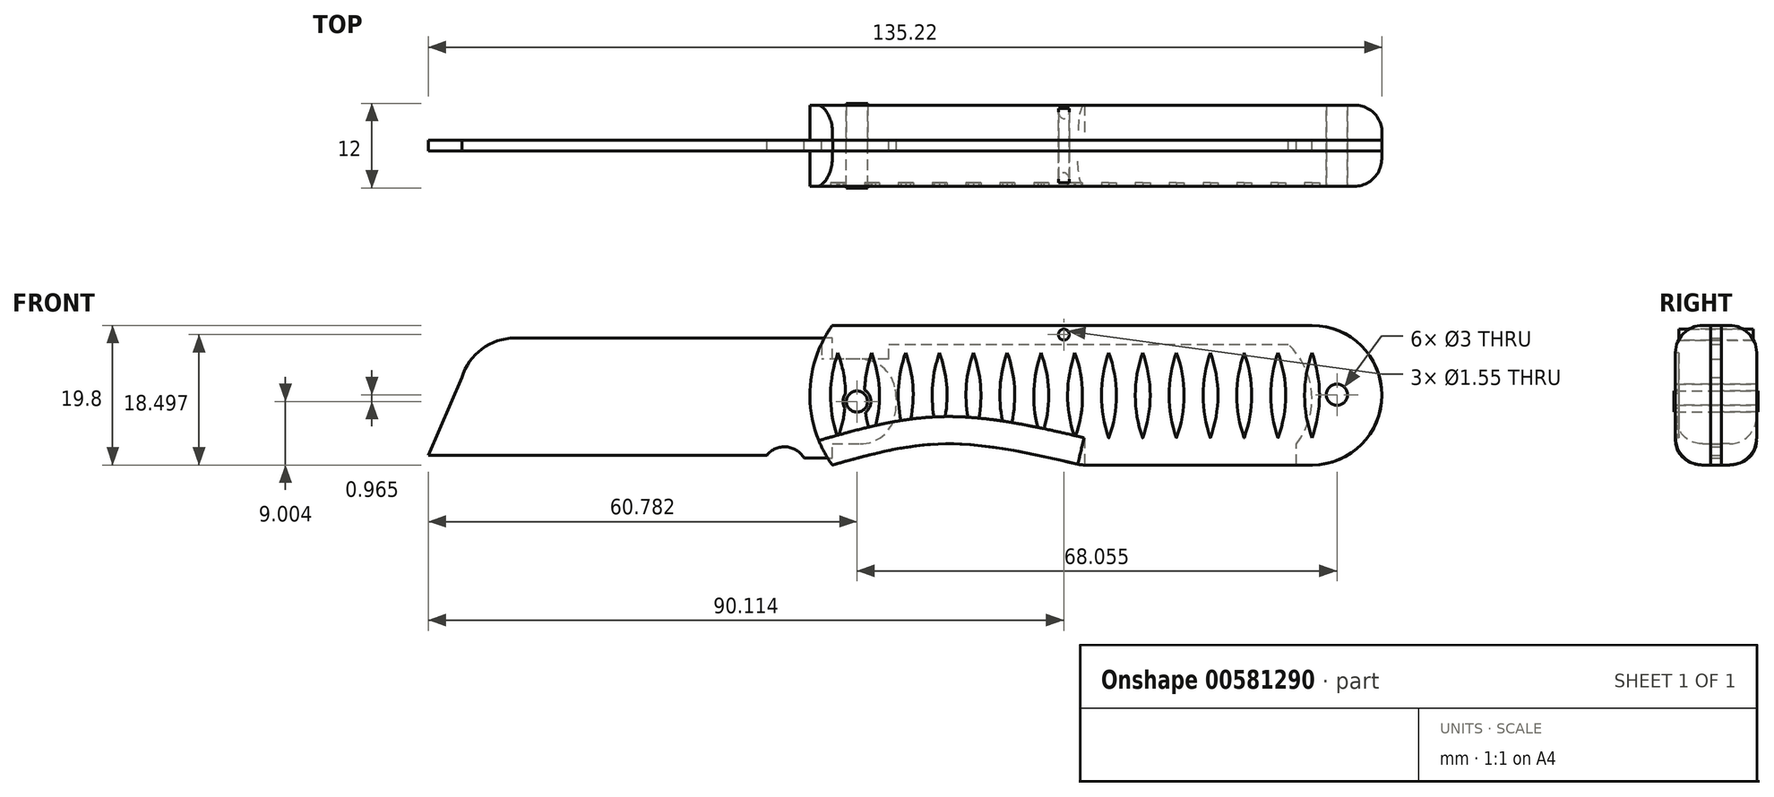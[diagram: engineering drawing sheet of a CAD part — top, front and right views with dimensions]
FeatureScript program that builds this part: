
annotation { "Feature Type Name" : "Feature", "Feature Type Description" : "" }
export const myFeature = defineFeature(function(context is Context, id is Id, definition is map)
    precondition{}
    {
        {
            var Q0;
            Q0=qCreatedBy(makeId("Front.planeOp"),FACE);
            var sketch = newSketch(context, id + "F0", { "sketchPlane" : qUnion([Q0])});
            skLineSegment(sketch, "E0", {"start": v(-36.7, 0) * mm, "end": v(11.3, 0) * mm});
            skArc(sketch, "E1", {"start": v(16.58, -0.4) * mm, "mid": v(14.04, 1.17) * mm, "end": v(11.3, 0) * mm});
            skLineSegment(sketch, "E2", {"start": v(16.58, -0.4) * mm, "end": v(20.58, -0.4) * mm});
            skLineSegment(sketch, "E3", {"start": v(20.58, -0.4) * mm, "end": v(20.58, 1.6) * mm});
            skLineSegment(sketch, "E4", {"start": v(20.58, 1.6) * mm, "end": v(27.58, 1.6) * mm});
            skLineSegment(sketch, "E5", {"start": v(27.58, 13.6) * mm, "end": v(20.58, 13.6) * mm});
            skArc(sketch, "E6", {"start": v(27.58, 1.6) * mm, "mid": v(29.67, 7.6) * mm, "end": v(27.58, 13.6) * mm});
            skLineSegment(sketch, "E7", {"start": v(20.58, 13.6) * mm, "end": v(20.58, 16.6) * mm});
            skCircle(sketch, "E8", {"center": v(24.08, 7.6) * mm, "radius": 1.5 * mm});
            skLineSegment(sketch, "E9", {"start": v(20.58, 16.6) * mm, "end": v(-24.42, 16.6) * mm});
            skArc(sketch, "E10", {"start": v(-24.42, 16.6) * mm, "mid": v(-29.1, 15.05) * mm, "end": v(-31.92, 11) * mm});
            skLineSegment(sketch, "E11", {"start": v(-31.92, 11) * mm, "end": v(-36.7, 0) * mm});
            skPoint(sketch, "E12.end.orphan", {"position": v(16.3, 0) * mm});
            skPoint(sketch, "E13.orphan", {"position": v(24.08, 13.6) * mm});
            skSolve(sketch);
        }
        {
            var Q0;
            Q0 = qSketchRegion(id + "F0", true);
            extrude(context, id + "F1", {"entities" : qUnion([Q0]), "endBound" : BoundingType.SYMMETRIC, "depth" : 1.5 * mm, "offsetDistance" : 25 * mm});
        }
        {
            var Q0;
            Q0=makeQuery(id+"F1.opExtrude","CAP_FACE",FACE,{"disambiguationData":[OSD([sQuery(id+"F0.wireOp",EDGE,"E0"),sQuery(id+"F0.wireOp",EDGE,"E1"),sQuery(id+"F0.wireOp",EDGE,"E2"),sQuery(id+"F0.wireOp",EDGE,"E3"),sQuery(id+"F0.wireOp",EDGE,"E4"),sQuery(id+"F0.wireOp",EDGE,"E5"),sQuery(id+"F0.wireOp",EDGE,"E6"),sQuery(id+"F0.wireOp",EDGE,"E7"),sQuery(id+"F0.wireOp",EDGE,"E8"),sQuery(id+"F0.wireOp",EDGE,"E9"),sQuery(id+"F0.wireOp",EDGE,"E10"),sQuery(id+"F0.wireOp",EDGE,"E11")])],"isStart":false});
            var sketch = newSketch(context, id + "F2", { "sketchPlane" : qUnion([Q0])});
            skCircle(sketch, "E14", {"center": v(24.08, 7.6) * mm, "radius": 1.5 * mm});
            skLineSegment(sketch, "E15", {"start": v(17.43, 7.6) * mm, "end": v(33.27, 7.6) * mm});
            skPoint(sketch, "E16.MirrorCS.end.orphan", {"position": v(17.43, 7.6) * mm});
            skLineSegment(sketch, "E17", {"start": v(55.83, -1.4) * mm, "end": v(88.58, -1.4) * mm});
            skFitSpline(sketch, "E18", {"points": [v(20.58, -1.4) * mm, v(36.47, 1.6) * mm, v(55.83, -1.4) * mm], "startDerivative": vector(32.52, 9.17) * mm, "endDerivative": vector(37.9, -8.88) * mm});
            skLineSegment(sketch, "E19.MirrorCS", {"start": v(20.58, 18.4) * mm, "end": v(88.58, 18.4) * mm});
            skArc(sketch, "E20", {"start": v(20.58, 18.4) * mm, "mid": v(17.4, 8.5) * mm, "end": v(20.58, -1.4) * mm});
            skArc(sketch, "E21", {"start": v(88.58, -1.4) * mm, "mid": v(98.48, 8.5) * mm, "end": v(88.58, 18.4) * mm});
            skSolve(sketch);
        }
        {
            var Q0;
            Q0 = qSketchRegion(id + "F2", true);
            extrude(context, id + "F3", {"entities" : qUnion([Q0]), "depth" : 5 * mm, "offsetDistance" : 25 * mm});
        }
        {
            var Q0;
            Q0=makeQuery(id+"F3.opExtrude","CAP_EDGE",EDGE,{"disambiguationData":[OSD([sQuery(id+"F2.wireOp",EDGE,"E18")])],"isStart":false});
            fillet(context, id + "F4", {"entities" : qUnion([Q0]), "radius" : 3.86 * mm, "tangentPropagation" : true, "allowEdgeOverflow" : false});
        }
        {
            var Q0;
            Q0=makeQuery(id+"F3.opExtrude","CAP_EDGE",EDGE,{"disambiguationData":[OSD([sQuery(id+"F2.wireOp",EDGE,"E17")])],"isStart":false});
            fillet(context, id + "F5", {"entities" : qUnion([Q0]), "radius" : 3.86 * mm, "tangentPropagation" : true, "allowEdgeOverflow" : false});
        }
        {
            var Q0;
            Q0=makeQuery(id+"F1.opExtrude","CAP_FACE",FACE,{"disambiguationData":[OSD([sQuery(id+"F0.wireOp",EDGE,"E0"),sQuery(id+"F0.wireOp",EDGE,"E1"),sQuery(id+"F0.wireOp",EDGE,"E2"),sQuery(id+"F0.wireOp",EDGE,"E3"),sQuery(id+"F0.wireOp",EDGE,"E4"),sQuery(id+"F0.wireOp",EDGE,"E5"),sQuery(id+"F0.wireOp",EDGE,"E6"),sQuery(id+"F0.wireOp",EDGE,"E7"),sQuery(id+"F0.wireOp",EDGE,"E8"),sQuery(id+"F0.wireOp",EDGE,"E9"),sQuery(id+"F0.wireOp",EDGE,"E10"),sQuery(id+"F0.wireOp",EDGE,"E11")])],"isStart":true});
            var sketch = newSketch(context, id + "F6", { "sketchPlane" : qUnion([Q0])});
            skCircle(sketch, "E22.MirrorC", {"center": v(-24.08, 7.6) * mm, "radius": 1.5 * mm});
            skLineSegment(sketch, "E23.MirrorCS", {"start": v(-55.87, -1.4) * mm, "end": v(-88.62, -1.4) * mm});
            skFitSpline(sketch, "E24.MirrorCS", {"points": [v(-20.62, -1.4) * mm, v(-36.5, 1.6) * mm, v(-55.87, -1.4) * mm], "startDerivative": vector(-32.52, 9.17) * mm, "endDerivative": vector(-37.9, -8.88) * mm});
            skLineSegment(sketch, "E25.MirrorCS", {"start": v(-20.62, 18.4) * mm, "end": v(-88.62, 18.4) * mm});
            skArc(sketch, "E26.MirrorCS", {"start": v(-20.62, 18.4) * mm, "mid": v(-17.45, 8.5) * mm, "end": v(-20.62, -1.4) * mm});
            skArc(sketch, "E27.MirrorCS", {"start": v(-88.62, -1.4) * mm, "mid": v(-98.52, 8.5) * mm, "end": v(-88.62, 18.4) * mm});
            skLineSegment(sketch, "E28.MirrorCS", {"start": v(-17.47, 7.6) * mm, "end": v(-33.31, 7.6) * mm});
            skSolve(sketch);
        }
        {
            var Q0;
            Q0 = qSketchRegion(id + "F6", true);
            extrude(context, id + "F7", {"entities" : qUnion([Q0]), "depth" : 5 * mm, "offsetDistance" : 25 * mm});
        }
        {
            var Q0;
            Q0=makeQuery(id+"F7.opExtrude","CAP_EDGE",EDGE,{"disambiguationData":[OSD([sQuery(id+"F6.wireOp",EDGE,"a4459e08-6a74-43f8-8a37-8007887f801a2.MirrorCS")])],"isStart":false});
            var Q1;
            Q1=makeQuery(id+"F7.opExtrude","CAP_EDGE",EDGE,{"disambiguationData":[OSD([sQuery(id+"F6.wireOp",EDGE,"205b8de5-6952-42f7-a2c1-d582361c57c33.MirrorCS")])],"isStart":false});
            var Q2;
            Q2=makeQuery(id+"F7.opExtrude","CAP_EDGE",EDGE,{"disambiguationData":[OSD([sQuery(id+"F6.wireOp",EDGE,"E24.MirrorCS")])],"isStart":false});
            fillet(context, id + "F8", {"entities" : qUnion([Q0, Q1, Q2]), "radius" : 3.86 * mm, "tangentPropagation" : true, "allowEdgeOverflow" : false});
        }
        {
            var Q0;
            Q0=makeQuery(id+"F7.opExtrude","CAP_EDGE",EDGE,{"disambiguationData":[OSD([sQuery(id+"F6.wireOp",EDGE,"a4459e08-6a74-43f8-8a37-8007887f801a3.MirrorCS")])],"isStart":false});
            var Q1;
            Q1=makeQuery(id+"F7.opExtrude","CAP_EDGE",EDGE,{"disambiguationData":[OSD([sQuery(id+"F6.wireOp",EDGE,"205b8de5-6952-42f7-a2c1-d582361c57c32.MirrorCS")])],"isStart":false});
            var Q2;
            Q2=makeQuery(id+"F7.opExtrude","CAP_EDGE",EDGE,{"disambiguationData":[OSD([sQuery(id+"F6.wireOp",EDGE,"E23.MirrorCS")])],"isStart":false});
            fillet(context, id + "F9", {"entities" : qUnion([Q0, Q1, Q2]), "radius" : 3.86 * mm, "tangentPropagation" : true, "allowEdgeOverflow" : false});
        }
        {
            var Q0;
            Q0=makeQuery(id+"F0.imprint","IMPRINT",FACE,{"disambiguationData":[TD([[makeQuery(id+"F0.imprint","IMPRINT",EDGE,{"derivedFrom":sQuery(id+"F0.wireOp",EDGE,"E8")}),1.0]])]});
            extrude(context, id + "F10", {"entities" : qUnion([Q0]), "endBound" : BoundingType.SYMMETRIC, "depth" : 12 * mm, "offsetDistance" : 25 * mm});
        }
        {
            var Q0;
            Q0=qCreatedBy(makeId("Front.planeOp"),FACE);
            var sketch = newSketch(context, id + "F11", { "sketchPlane" : qUnion([Q0])});
            skLineSegment(sketch, "E29", {"start": v(22.62, 18.4) * mm, "end": v(84.2, 18.4) * mm});
            skPoint(sketch, "E30.orphan", {"position": v(53.4, 18.4) * mm});
            skPoint(sketch, "E31.end.orphan", {"position": v(87.09, 16.63) * mm});
            skLineSegment(sketch, "E32", {"start": v(84.2, 18.4) * mm, "end": v(88.58, 18.4) * mm});
            skArc(sketch, "E33", {"start": v(88.58, -1.4) * mm, "mid": v(98.48, 8.5) * mm, "end": v(88.58, 18.4) * mm});
            skLineSegment(sketch, "E34", {"start": v(20.58, 13.6) * mm, "end": v(27.58, 13.6) * mm});
            skLineSegment(sketch, "E35", {"start": v(28.58, 15.72) * mm, "end": v(84.2, 15.72) * mm});
            skLineSegment(sketch, "E36", {"start": v(86.4, -1.4) * mm, "end": v(88.58, -1.4) * mm});
            skLineSegment(sketch, "E37", {"start": v(86.4, -1.4) * mm, "end": v(86.4, 1.57) * mm});
            skPoint(sketch, "E38.orphan", {"position": v(84.2, -1.4) * mm});
            skLineSegment(sketch, "E39", {"start": v(84.2, 15.72) * mm, "end": v(85.2, 15.72) * mm});
            skArc(sketch, "E40", {"start": v(86.4, 1.57) * mm, "mid": v(88.56, 8.87) * mm, "end": v(85.2, 15.72) * mm});
            skLineSegment(sketch, "E41", {"start": v(20.58, 13.6) * mm, "end": v(19.04, 13.6) * mm});
            skPoint(sketch, "E42.start.orphan", {"position": v(20.58, 16.6) * mm});
            skLineSegment(sketch, "E43", {"start": v(27.58, 13.6) * mm, "end": v(28.58, 13.6) * mm});
            skLineSegment(sketch, "E44", {"start": v(28.58, 13.6) * mm, "end": v(28.58, 15.72) * mm});
            skPoint(sketch, "E45.end.orphan", {"position": v(18.58, 16.6) * mm});
            skLineSegment(sketch, "E46", {"start": v(22.62, 18.4) * mm, "end": v(20.65, 18.4) * mm});
            skLineSegment(sketch, "E47", {"start": v(19.04, 15.72) * mm, "end": v(19.04, 13.6) * mm});
            skPoint(sketch, "E48.orphan", {"position": v(18.58, 13.6) * mm});
            skArc(sketch, "E49", {"start": v(20.65, 18.4) * mm, "mid": v(19.78, 17.1) * mm, "end": v(19.04, 15.72) * mm});
            skSolve(sketch);
        }
        {
            var Q0;
            Q0 = qSketchRegion(id + "F11", true);
            extrude(context, id + "F12", {"entities" : qUnion([Q0]), "endBound" : BoundingType.SYMMETRIC, "depth" : 1.5 * mm, "offsetDistance" : 25 * mm});
        }
        {
            var Q0;
            Q0=qCreatedBy(makeId("Front.planeOp"),FACE);
            var sketch = newSketch(context, id + "F13", { "sketchPlane" : qUnion([Q0])});
            skCircle(sketch, "E50", {"center": v(53.41, 17.1) * mm, "radius": 0.78 * mm});
            skSolve(sketch);
        }
        {
            var Q0;
            Q0 = qSketchRegion(id + "F13", true);
            extrude(context, id + "F14", {"entities" : qUnion([Q0]), "operationType" : NewBodyOperationType.REMOVE, "endBound" : BoundingType.SYMMETRIC, "oppositeDirection" : true, "depth" : 25 * mm, "offsetDistance" : 25 * mm});
        }
        {
            var Q0;
            Q0 = qSketchRegion(id + "F13", true);
            extrude(context, id + "F15", {"entities" : qUnion([Q0]), "endBound" : BoundingType.SYMMETRIC, "depth" : 10.54 * mm, "offsetDistance" : 25 * mm});
        }
        {
            var Q0;
            Q0=makeQuery(id+"F1.opExtrude","SWEPT_EDGE",EDGE,{"disambiguationData":[OSD([sQuery(id+"F0.wireOp",EDGE,"E5"),sQuery(id+"F0.wireOp",EDGE,"E6")])]});
            var Q1;
            Q1=makeQuery(id+"F1.opExtrude","SWEPT_EDGE",EDGE,{"disambiguationData":[OSD([sQuery(id+"F0.wireOp",EDGE,"E4"),sQuery(id+"F0.wireOp",EDGE,"E6")])]});
            fillet(context, id + "F16", {"entities" : qUnion([Q0, Q1]), "radius" : 5 * mm, "tangentPropagation" : true, "allowEdgeOverflow" : false});
        }
        {
            var Q0;
            Q0=qCreatedBy(makeId("Front.planeOp"),FACE);
            var sketch = newSketch(context, id + "F17", { "sketchPlane" : qUnion([Q0])});
            skCircle(sketch, "E51", {"center": v(92.14, 8.57) * mm, "radius": 1.5 * mm});
            skSolve(sketch);
        }
        {
            var Q0;
            Q0 = qSketchRegion(id + "F17", true);
            extrude(context, id + "F18", {"entities" : qUnion([Q0]), "operationType" : NewBodyOperationType.REMOVE, "endBound" : BoundingType.SYMMETRIC, "oppositeDirection" : true, "depth" : 25 * mm, "offsetDistance" : 25 * mm});
        }
        {
            var Q0;
            Q0 = qSketchRegion(id + "F17", true);
            extrude(context, id + "F19", {"entities" : qUnion([Q0]), "endBound" : BoundingType.SYMMETRIC, "depth" : 11.5 * mm, "offsetDistance" : 25 * mm});
        }
        {
            var Q0;
            Q0=makeQuery(id+"F3.opExtrude","CAP_FACE",FACE,{"disambiguationData":[OSD([sQuery(id+"F2.wireOp",EDGE,"E14"),sQuery(id+"F2.wireOp",EDGE,"E17"),sQuery(id+"F2.wireOp",EDGE,"E18"),sQuery(id+"F2.wireOp",EDGE,"E19.MirrorCS"),sQuery(id+"F2.wireOp",EDGE,"E20"),sQuery(id+"F2.wireOp",EDGE,"E21")])],"isStart":false});
            var sketch = newSketch(context, id + "F20", { "sketchPlane" : qUnion([Q0])});
            skArc(sketch, "E52", {"start": v(88.58, 2.47) * mm, "mid": v(89.66, 8.5) * mm, "end": v(88.58, 14.54) * mm});
            skArc(sketch, "E53", {"start": v(88.58, 14.54) * mm, "mid": v(87.54, 8.5) * mm, "end": v(88.58, 2.47) * mm});
            skArc(sketch, "E54.1.0.0", {"start": v(83.78, 2.46) * mm, "mid": v(84.86, 8.5) * mm, "end": v(83.78, 14.54) * mm});
            skArc(sketch, "E54.1.0.1", {"start": v(83.78, 14.54) * mm, "mid": v(82.74, 8.5) * mm, "end": v(83.78, 2.46) * mm});
            skArc(sketch, "E54.2.0.0", {"start": v(78.98, 2.46) * mm, "mid": v(80.06, 8.5) * mm, "end": v(78.98, 14.53) * mm});
            skArc(sketch, "E54.2.0.1", {"start": v(78.98, 14.53) * mm, "mid": v(77.94, 8.5) * mm, "end": v(78.98, 2.46) * mm});
            skArc(sketch, "E54.3.0.0", {"start": v(74.18, 2.46) * mm, "mid": v(75.26, 8.5) * mm, "end": v(74.18, 14.53) * mm});
            skArc(sketch, "E54.3.0.1", {"start": v(74.18, 14.53) * mm, "mid": v(73.14, 8.5) * mm, "end": v(74.18, 2.46) * mm});
            skArc(sketch, "E54.4.0.0", {"start": v(69.38, 2.45) * mm, "mid": v(70.46, 8.49) * mm, "end": v(69.38, 14.53) * mm});
            skArc(sketch, "E54.4.0.1", {"start": v(69.38, 14.53) * mm, "mid": v(68.34, 8.49) * mm, "end": v(69.38, 2.45) * mm});
            skArc(sketch, "E54.5.0.0", {"start": v(64.58, 2.45) * mm, "mid": v(65.66, 8.48) * mm, "end": v(64.58, 14.52) * mm});
            skArc(sketch, "E54.5.0.1", {"start": v(64.58, 14.52) * mm, "mid": v(63.54, 8.48) * mm, "end": v(64.58, 2.45) * mm});
            skArc(sketch, "E54.6.0.0", {"start": v(59.78, 2.44) * mm, "mid": v(60.86, 8.48) * mm, "end": v(59.78, 14.52) * mm});
            skArc(sketch, "E54.6.0.1", {"start": v(59.78, 14.52) * mm, "mid": v(58.74, 8.48) * mm, "end": v(59.78, 2.44) * mm});
            skArc(sketch, "E54.7.0.0", {"start": v(55.1, 2.74) * mm, "mid": v(56.06, 8.64) * mm, "end": v(54.98, 14.51) * mm});
            skArc(sketch, "E54.7.0.1", {"start": v(54.98, 14.51) * mm, "mid": v(53.94, 8.67) * mm, "end": v(54.86, 2.8) * mm});
            skArc(sketch, "E54.8.0.0", {"start": v(50.6, 3.75) * mm, "mid": v(51.25, 9.16) * mm, "end": v(50.18, 14.51) * mm});
            skArc(sketch, "E54.8.0.1", {"start": v(50.18, 14.51) * mm, "mid": v(49.16, 9.26) * mm, "end": v(49.72, 3.94) * mm});
            skArc(sketch, "E54.9.0.0", {"start": v(46.03, 4.63) * mm, "mid": v(46.42, 9.62) * mm, "end": v(45.38, 14.5) * mm});
            skArc(sketch, "E54.9.0.1", {"start": v(45.38, 14.5) * mm, "mid": v(44.39, 9.72) * mm, "end": v(44.71, 4.84) * mm});
            skArc(sketch, "E54.10.0.0", {"start": v(41.36, 5.26) * mm, "mid": v(41.6, 9.93) * mm, "end": v(40.58, 14.5) * mm});
            skArc(sketch, "E54.10.0.1", {"start": v(40.58, 14.5) * mm, "mid": v(39.6, 10) * mm, "end": v(39.8, 5.38) * mm});
            skArc(sketch, "E54.11.0.0", {"start": v(36.6, 5.47) * mm, "mid": v(36.79, 10.04) * mm, "end": v(35.78, 14.5) * mm});
            skArc(sketch, "E54.11.0.1", {"start": v(35.78, 14.5) * mm, "mid": v(34.8, 10) * mm, "end": v(35, 5.42) * mm});
            skArc(sketch, "E54.12.0.0", {"start": v(31.74, 5.11) * mm, "mid": v(32, 9.86) * mm, "end": v(30.98, 14.5) * mm});
            skArc(sketch, "E54.12.0.1", {"start": v(30.98, 14.5) * mm, "mid": v(29.99, 9.75) * mm, "end": v(30.3, 4.9) * mm});
            skArc(sketch, "E54.13.0.0", {"start": v(26.74, 4.21) * mm, "mid": v(27.23, 9.4) * mm, "end": v(26.18, 14.5) * mm});
            skArc(sketch, "E54.13.0.1", {"start": v(26.18, 14.5) * mm, "mid": v(25.47, 11.87) * mm, "end": v(25.16, 9.17) * mm});
            skArc(sketch, "E54.14.0.0", {"start": v(21.55, 2.89) * mm, "mid": v(22.06, 4.73) * mm, "end": v(22.36, 6.63) * mm});
            skArc(sketch, "E54.14.0.1", {"start": v(21.38, 14.49) * mm, "mid": v(20.34, 8.66) * mm, "end": v(21.25, 2.8) * mm});
            skLineSegment(sketch, "E54.direction1", {"start": v(72.22, 8.5) * mm, "end": v(67.42, 8.5) * mm, "construction": true});
            skArc(sketch, "E55.trimOffspring", {"start": v(25.3, 6.05) * mm, "mid": v(25.48, 5) * mm, "end": v(25.7, 3.97) * mm});
            skLineSegment(sketch, "E56", {"start": v(25.7, 3.97) * mm, "end": v(26.74, 4.21) * mm});
            skPoint(sketch, "E57.orphan", {"position": v(26.18, 2.42) * mm});
            skArc(sketch, "E58", {"start": v(22.46, 8.73) * mm, "mid": v(22.1, 7.7) * mm, "end": v(22.36, 6.63) * mm});
            skArc(sketch, "E59.trimOffspring", {"start": v(22.46, 8.73) * mm, "mid": v(22.16, 11.65) * mm, "end": v(21.38, 14.49) * mm});
            skArc(sketch, "E60.trimOffspring", {"start": v(25.3, 6.05) * mm, "mid": v(26.06, 7.7) * mm, "end": v(25.16, 9.26) * mm});
            skLineSegment(sketch, "E61", {"start": v(21.25, 2.8) * mm, "end": v(21.55, 2.89) * mm});
            skPoint(sketch, "E62.orphan", {"position": v(21.38, 2.41) * mm});
            skLineSegment(sketch, "E63", {"start": v(30.3, 4.9) * mm, "end": v(31.74, 5.11) * mm});
            skPoint(sketch, "E64.orphan", {"position": v(30.98, 2.42) * mm});
            skLineSegment(sketch, "E65", {"start": v(35, 5.42) * mm, "end": v(36.6, 5.47) * mm});
            skPoint(sketch, "E66.orphan", {"position": v(35.78, 2.42) * mm});
            skLineSegment(sketch, "E67", {"start": v(39.8, 5.38) * mm, "end": v(41.36, 5.26) * mm});
            skPoint(sketch, "E68.orphan", {"position": v(40.58, 2.43) * mm});
            skLineSegment(sketch, "E69", {"start": v(44.71, 4.84) * mm, "end": v(46.03, 4.63) * mm});
            skPoint(sketch, "E70.orphan", {"position": v(45.38, 2.43) * mm});
            skLineSegment(sketch, "E71", {"start": v(49.72, 3.94) * mm, "end": v(50.6, 3.75) * mm});
            skPoint(sketch, "E72.orphan", {"position": v(50.18, 2.44) * mm});
            skLineSegment(sketch, "E73", {"start": v(54.86, 2.8) * mm, "end": v(55.1, 2.74) * mm});
            skPoint(sketch, "E74.orphan", {"position": v(54.98, 2.44) * mm});
            skSolve(sketch);
        }
        {
            var Q0;
            Q0 = qSketchRegion(id + "F20", true);
            extrude(context, id + "F21", {"entities" : qUnion([Q0]), "operationType" : NewBodyOperationType.REMOVE, "oppositeDirection" : true, "depth" : .50 * mm, "offsetDistance" : 25 * mm});
        }
    });
